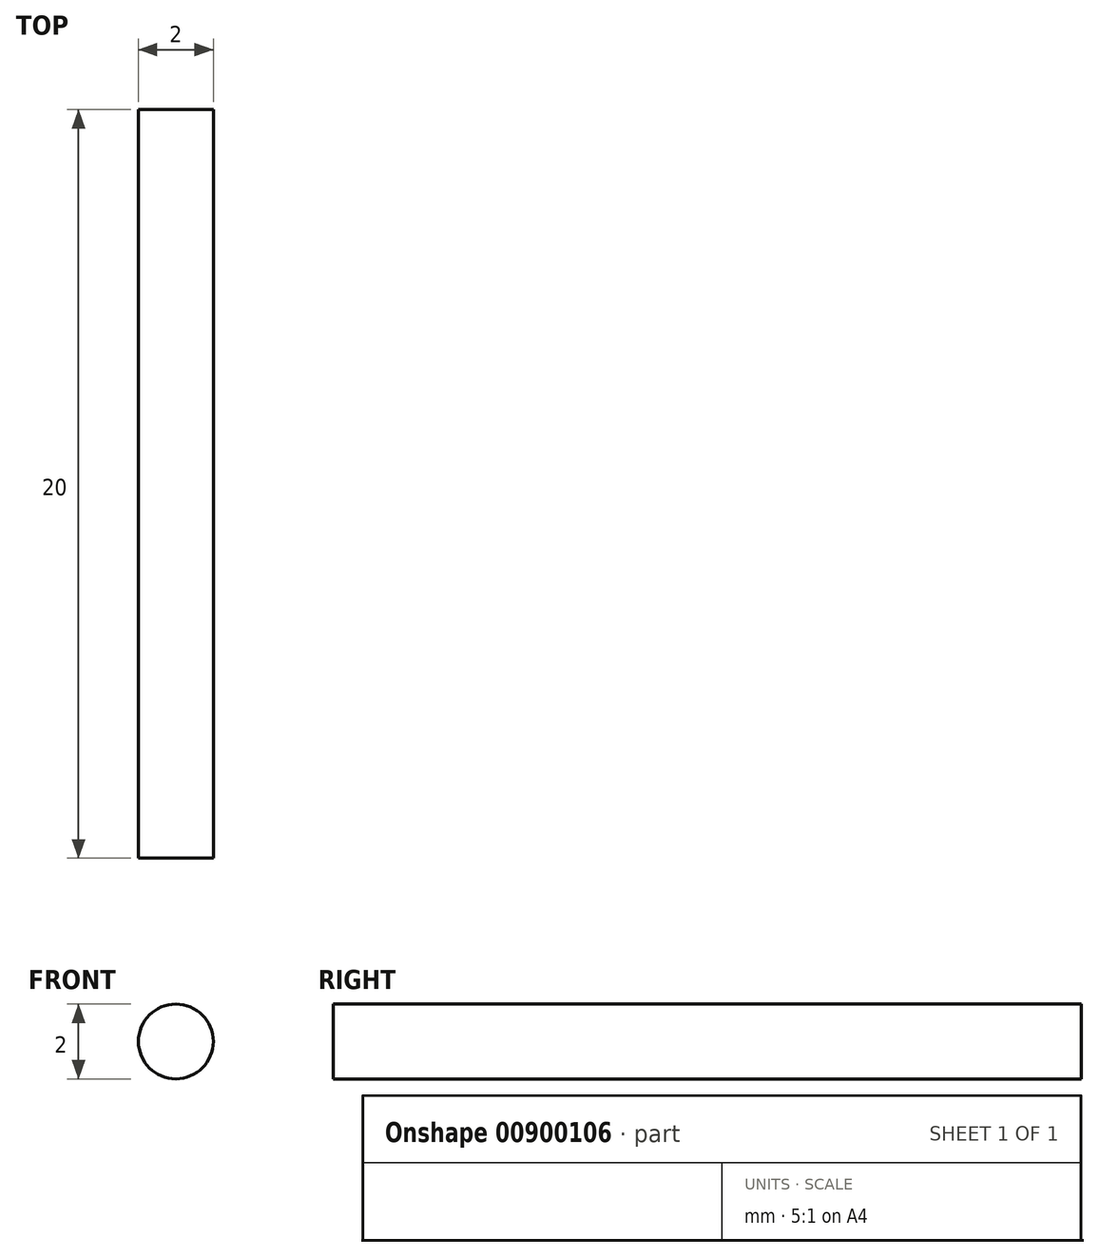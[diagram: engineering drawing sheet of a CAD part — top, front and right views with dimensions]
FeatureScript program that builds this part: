
annotation { "Feature Type Name" : "Feature", "Feature Type Description" : "" }
export const myFeature = defineFeature(function(context is Context, id is Id, definition is map)
    precondition{}
    {
        {
            var Q0;
            Q0=qCreatedBy(makeId("Front.planeOp"),FACE);
            var sketch = newSketch(context, id + "F0", { "sketchPlane" : qUnion([Q0])});
            skCircle(sketch, "E0", {"center": v(0, 0) * mm, "radius": 1 * mm});
            skSolve(sketch);
        }
        {
            var Q0;
            Q0 = qSketchRegion(id + "F0", true);
            extrude(context, id + "F1", {"entities" : qUnion([Q0]), "oppositeDirection" : true, "depth" : 20 * mm, "offsetDistance" : 25 * mm});
        }
    });
